# Revit family: 303_R27X_
name_source: partatom
category: Pipe Accessories
revit_build: Autodesk Revit 2018 (Build: 20170223_1515(x64)
units: mm (PartAtom-declared; Revit-internal decimal feet)

## family parameters
Always vertical = Yes
Cut with Voids When Loaded = No
Part Type = Valve - Breaks Into
Round Connector Dimension = Use Diameter
Shared = No
Work Plane-Based = No

## types (5) — shared parameters
CAT0 = Yes
Description = Manual straight valve, screwed ends
L2D_Min = 3048 mm
L5 = 4 mm  [stored 0.0131234 ft]
L62 = 2 mm  [stored 0.00656168 ft]
L62__ve = -2 mm  [stored -0.00656168 ft]
Manufacturer = Giacomini
QmdConnectorList = 301;D;302;D
SW2 = No
URL = http://www.giacomini.com
magiPartTypeId = 303
magiProductFamilyId = R27X*
zero-valued in all types: MC_Default_elevation

## per-type parameters (varying)
- R27X032: B3=9 mm  [stored 0.0295276 ft]; B4=6 mm  [stored 0.019685 ft]; CenSd_W2_6=13 mm; D=16 mm; G1=8 mm  [stored 0.0262467 ft]; G3=10 mm  [stored 0.0328084 ft]; J6=43 mm  [stored 0.141076 ft]; K3=9 mm  [stored 0.0295276 ft]; L2=9 mm  [stored 0.0295276 ft]; L2D=56 mm; L6=4 mm  [stored 0.0131234 ft]; L6__ve=-4 mm  [stored -0.0131234 ft]; L8=2 mm  [stored 0.00656168 ft]; L8__ve=-2 mm  [stored -0.00656168 ft]; L9=6 mm  [stored 0.019685 ft]; L9__ve=-6 mm; LC=52 mm  [stored 0.170604 ft]; LC1=28 mm  [stored 0.0918635 ft]; LC2=37 mm; LX=34 mm; M1=21 mm  [stored 0.0688976 ft]; R1=8 mm  [stored 0.0262467 ft]; SW1=Yes; SW3=Yes; SW4=No; W2=15 mm  [stored 0.0492126 ft]; W2D=16 mm  [stored 0.0524934 ft]; W4=9 mm  [stored 0.0295276 ft]; X11=13 mm
- R27X036: B3=10 mm  [stored 0.0328084 ft]; B4=7 mm  [stored 0.0229659 ft]; CenSd_W2_6=16 mm  [stored 0.0524934 ft]; D=22 mm; G1=13 mm; G3=15 mm  [stored 0.0492126 ft]; J6=49 mm; K3=10 mm  [stored 0.0328084 ft]; L2=10 mm  [stored 0.0328084 ft]; L2D=65 mm; L6=5 mm  [stored 0.0164042 ft]; L6__ve=-5 mm  [stored -0.0164042 ft]; L8=3 mm  [stored 0.00984252 ft]; L8__ve=-3 mm; L9=8 mm  [stored 0.0262467 ft]; L9__ve=-8 mm  [stored -0.0262467 ft]; LC=55 mm; LC1=33 mm; LC2=43 mm  [stored 0.141076 ft]; LX=41 mm; M1=25 mm  [stored 0.082021 ft]; R1=13 mm; SW1=No; SW3=No; SW4=Yes; W2=19 mm  [stored 0.062336 ft]; W2D=22 mm; W4=11 mm; X11=15 mm  [stored 0.0492126 ft]
- R27X035: B3=10 mm  [stored 0.0328084 ft]; B4=6 mm  [stored 0.019685 ft]; CenSd_W2_6=16 mm  [stored 0.0524934 ft]; D=18 mm; G1=13 mm; G3=15 mm  [stored 0.0492126 ft]; J6=49 mm; K3=10 mm  [stored 0.0328084 ft]; L2=10 mm  [stored 0.0328084 ft]; L2D=65 mm; L6=5 mm  [stored 0.0164042 ft]; L6__ve=-5 mm  [stored -0.0164042 ft]; L8=3 mm  [stored 0.00984252 ft]; L8__ve=-3 mm; L9=8 mm  [stored 0.0262467 ft]; L9__ve=-8 mm  [stored -0.0262467 ft]; LC=55 mm; LC1=33 mm; LC2=43 mm  [stored 0.141076 ft]; LX=41 mm; M1=25 mm  [stored 0.082021 ft]; R1=13 mm; SW1=No; SW3=No; SW4=Yes; W2=19 mm  [stored 0.062336 ft]; W2D=18 mm  [stored 0.0590551 ft]; W4=11 mm; X11=15 mm  [stored 0.0492126 ft]
- R27X034: B3=10 mm  [stored 0.0328084 ft]; B4=6 mm  [stored 0.019685 ft]; CenSd_W2_6=13 mm; D=18 mm; G1=10 mm  [stored 0.0328084 ft]; G3=12 mm  [stored 0.0393701 ft]; J6=43 mm  [stored 0.141076 ft]; K3=10 mm  [stored 0.0328084 ft]; L2=9 mm  [stored 0.0295276 ft]; L2D=58 mm; L6=4 mm  [stored 0.0131234 ft]; L6__ve=-4 mm  [stored -0.0131234 ft]; L8=2 mm  [stored 0.00656168 ft]; L8__ve=-2 mm  [stored -0.00656168 ft]; L9=7 mm  [stored 0.0229659 ft]; L9__ve=-7 mm; LC=52 mm  [stored 0.170604 ft]; LC1=29 mm; LC2=39 mm; LX=35 mm; M1=21 mm  [stored 0.0688976 ft]; R1=11 mm; SW1=No; SW3=No; SW4=Yes; W2=15 mm  [stored 0.0492126 ft]; W2D=18 mm  [stored 0.0590551 ft]; W4=9 mm  [stored 0.0295276 ft]; X11=13 mm
- R27X033: B3=9 mm  [stored 0.0295276 ft]; B4=6 mm  [stored 0.019685 ft]; CenSd_W2_6=13 mm; D=16 mm; G1=10 mm  [stored 0.0328084 ft]; G3=12 mm  [stored 0.0393701 ft]; J6=43 mm  [stored 0.141076 ft]; K3=9 mm  [stored 0.0295276 ft]; L2=9 mm  [stored 0.0295276 ft]; L2D=57 mm; L6=4 mm  [stored 0.0131234 ft]; L6__ve=-4 mm  [stored -0.0131234 ft]; L8=2 mm  [stored 0.00656168 ft]; L8__ve=-2 mm  [stored -0.00656168 ft]; L9=7 mm  [stored 0.0229659 ft]; L9__ve=-7 mm; LC=52 mm  [stored 0.170604 ft]; LC1=29 mm; LC2=38 mm; LX=35 mm; M1=21 mm  [stored 0.0688976 ft]; R1=11 mm; SW1=Yes; SW3=Yes; SW4=No; W2=15 mm  [stored 0.0492126 ft]; W2D=16 mm  [stored 0.0524934 ft]; W4=9 mm  [stored 0.0295276 ft]; X11=13 mm

note: column(s) folded — value = type name in every type: magiProductCode, magiProductId

note: [stored X ft] marks values corroborated as IEEE doubles in the binary element streams (Revit-internal decimal feet)

## geometry (parser evidence)
native form markers: Sweep x2
no freeform markers — native parametric forms only
